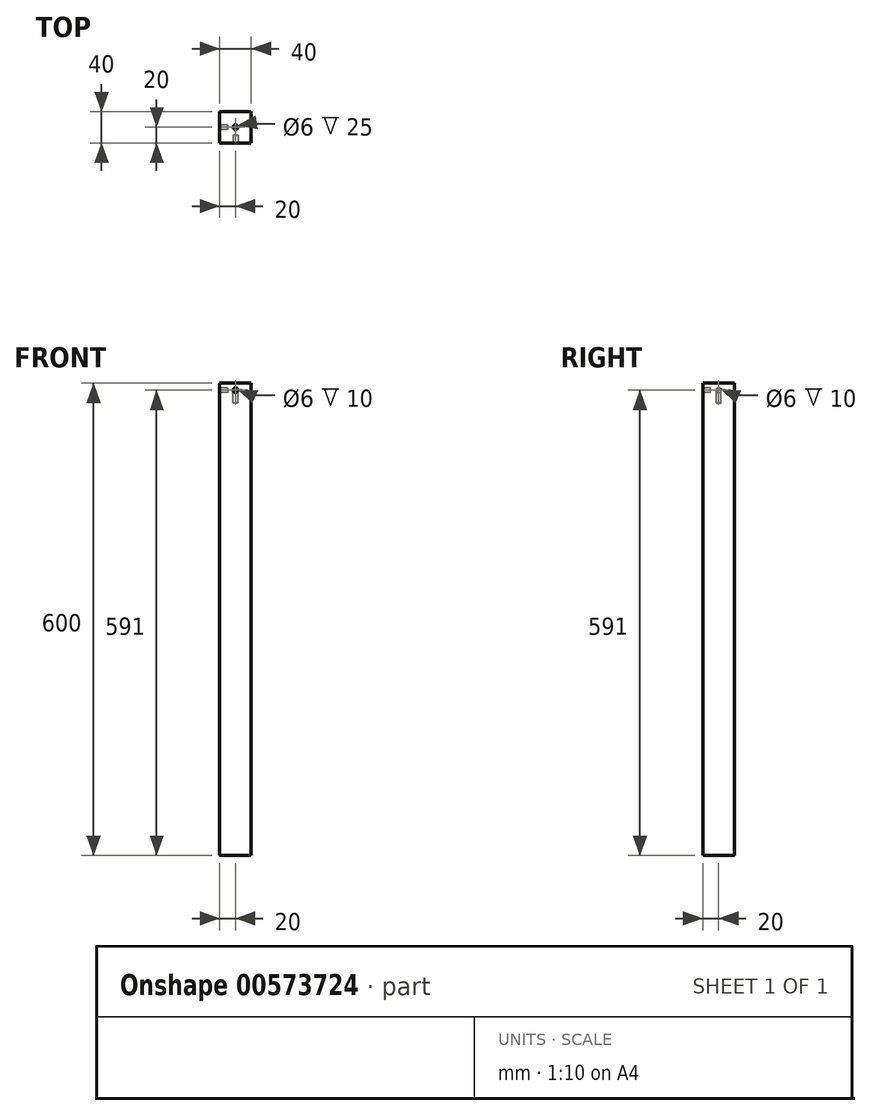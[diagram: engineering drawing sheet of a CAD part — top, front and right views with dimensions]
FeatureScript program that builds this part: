
annotation { "Feature Type Name" : "Feature", "Feature Type Description" : "" }
export const myFeature = defineFeature(function(context is Context, id is Id, definition is map)
    precondition{}
    {
        {
            var Q0;
            Q0=qCreatedBy(makeId("Top.planeOp"),FACE);
            var sketch = newSketch(context, id + "F0", { "sketchPlane" : qUnion([Q0])});
            skLineSegment(sketch, "E0.bottom", {"start": v(0, 0) * mm, "end": v(40, 0) * mm});
            skLineSegment(sketch, "E0.top", {"start": v(0, 40) * mm, "end": v(40, 40) * mm});
            skLineSegment(sketch, "E0.left", {"start": v(0, 0) * mm, "end": v(0, 40) * mm});
            skLineSegment(sketch, "E0.right", {"start": v(40, 0) * mm, "end": v(40, 40) * mm});
            skSolve(sketch);
        }
        {
            var Q0;
            Q0=makeQuery(id+"F0.imprint","IMPRINT",FACE,{"disambiguationData":[TD([[makeQuery(id+"F0.imprint","IMPRINT",EDGE,{"derivedFrom":sQuery(id+"F0.wireOp",EDGE,"E0.bottom")}),1.0]])]});
            extrude(context, id + "F1", {"entities" : qUnion([Q0]), "depth" : 600 * mm, "offsetDistance" : 25 * mm});
        }
        {
            var Q0;
            Q0=makeQuery(id+"F1.opExtrude","CAP_FACE",FACE,{"disambiguationData":[OSD([sQuery(id+"F0.wireOp",EDGE,"E0.bottom"),sQuery(id+"F0.wireOp",EDGE,"E0.top"),sQuery(id+"F0.wireOp",EDGE,"E0.left"),sQuery(id+"F0.wireOp",EDGE,"E0.right")])],"isStart":false});
            var sketch = newSketch(context, id + "F2", { "sketchPlane" : qUnion([Q0])});
            skCircle(sketch, "E1", {"center": v(20, 20) * mm, "radius": 3 * mm});
            skPoint(sketch, "E2", {"position": v(20, 40) * mm});
            skPoint(sketch, "E3", {"position": v(0, 20) * mm});
            skSolve(sketch);
        }
        {
            var Q0;
            Q0=qSketchRegion(id+"F2",true);
            extrude(context, id + "F3", {"entities" : qUnion([Q0]), "operationType" : NewBodyOperationType.REMOVE, "oppositeDirection" : true, "depth" : 25 * mm, "offsetDistance" : 25 * mm});
        }
        {
            var Q0;
            Q0=makeQuery(id+"F1.opExtrude","SWEPT_FACE",FACE,{"disambiguationData":[OSD([sQuery(id+"F0.wireOp",EDGE,"E0.bottom")])]});
            var sketch = newSketch(context, id + "F4", { "sketchPlane" : qUnion([Q0])});
            skCircle(sketch, "E4", {"center": v(20, 591) * mm, "radius": 3 * mm});
            skSolve(sketch);
        }
        {
            var Q0;
            Q0 = qSketchRegion(id + "F4", true);
            extrude(context, id + "F5", {"entities" : qUnion([Q0]), "operationType" : NewBodyOperationType.REMOVE, "oppositeDirection" : true, "depth" : 10 * mm, "offsetDistance" : 25 * mm});
        }
        {
            var Q0;
            Q0=makeQuery(id+"F1.opExtrude","SWEPT_FACE",FACE,{"disambiguationData":[OSD([sQuery(id+"F0.wireOp",EDGE,"E0.left")])]});
            var sketch = newSketch(context, id + "F6", { "sketchPlane" : qUnion([Q0])});
            skCircle(sketch, "E5", {"center": v(-20, 591) * mm, "radius": 3 * mm});
            skSolve(sketch);
        }
        {
            var Q0;
            Q0 = qSketchRegion(id + "F6", true);
            extrude(context, id + "F7", {"entities" : qUnion([Q0]), "operationType" : NewBodyOperationType.REMOVE, "oppositeDirection" : true, "depth" : 10 * mm, "offsetDistance" : 25 * mm});
        }
    });
